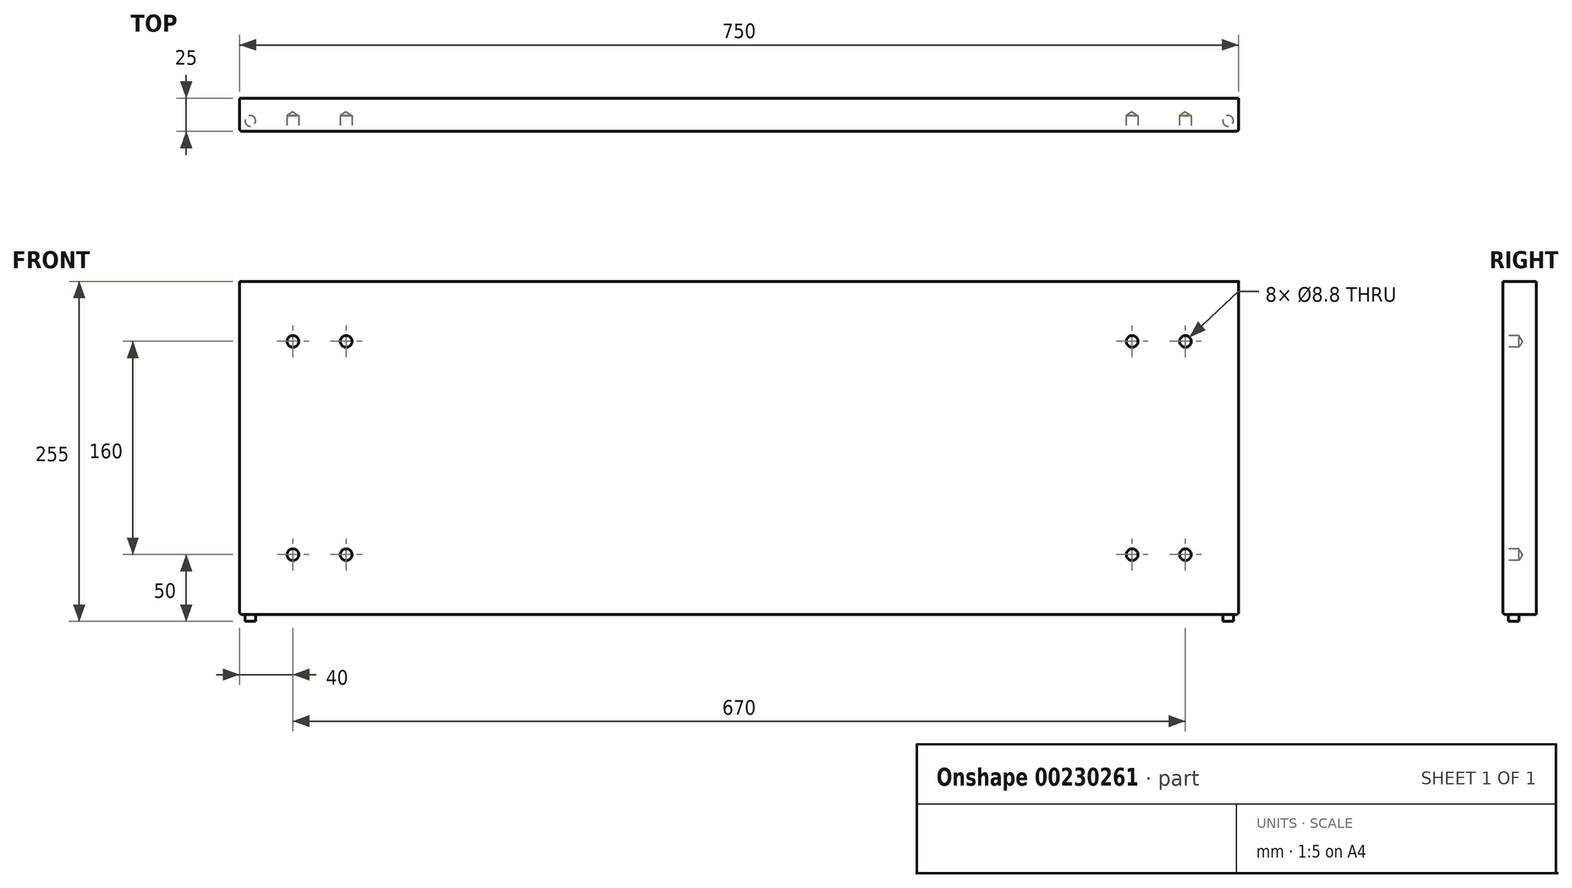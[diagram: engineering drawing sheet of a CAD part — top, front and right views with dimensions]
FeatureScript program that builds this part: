
annotation { "Feature Type Name" : "Feature", "Feature Type Description" : "" }
export const myFeature = defineFeature(function(context is Context, id is Id, definition is map)
    precondition{}
    {
        {
            var Q0;
            Q0=qCreatedBy(makeId("Front.planeOp"),FACE);
            var sketch = newSketch(context, id + "F0", { "sketchPlane" : qUnion([Q0])});
            skLineSegment(sketch, "E0.bottom", {"start": v(375, -125) * mm, "end": v(-375, -125) * mm});
            skLineSegment(sketch, "E0.top", {"start": v(375, 125) * mm, "end": v(-375, 125) * mm});
            skLineSegment(sketch, "E0.left", {"start": v(375, -125) * mm, "end": v(375, 125) * mm});
            skLineSegment(sketch, "E0.right", {"start": v(-375, -125) * mm, "end": v(-375, 125) * mm});
            skPoint(sketch, "E0.middle", {"position": v(0, 0) * mm});
            skSolve(sketch);
        }
        {
            var Q0;
            Q0=makeQuery(id+"F0.imprint","IMPRINT",FACE,{"disambiguationData":[TD([[makeQuery(id+"F0.imprint","IMPRINT",EDGE,{"derivedFrom":sQuery(id+"F0.wireOp",EDGE,"E0.bottom")}),-1.0]])]});
            extrude(context, id + "F1", {"entities" : qUnion([Q0]), "depth" : 25 * mm});
        }
        {
            var Q0;
            Q0=makeQuery(id+"F1.opExtrude","SWEPT_FACE",FACE,{"disambiguationData":[OSD([sQuery(id+"F0.wireOp",EDGE,"E0.bottom")])]});
            var sketch = newSketch(context, id + "F2", { "sketchPlane" : qUnion([Q0])});
            skCircle(sketch, "E1", {"center": v(-367, 17) * mm, "radius": 4 * mm});
            skCircle(sketch, "E2", {"center": v(367, 17) * mm, "radius": 4 * mm});
            skSolve(sketch);
        }
        {
            var Q0;
            Q0=makeQuery(id+"F2.imprint","IMPRINT",FACE,{"disambiguationData":[TD([[makeQuery(id+"F2.imprint","IMPRINT",EDGE,{"derivedFrom":sQuery(id+"F2.wireOp",EDGE,"E1")}),1.0]])]});
            var Q1;
            Q1=makeQuery(id+"F2.imprint","IMPRINT",FACE,{"disambiguationData":[TD([[makeQuery(id+"F2.imprint","IMPRINT",EDGE,{"derivedFrom":sQuery(id+"F2.wireOp",EDGE,"E2")}),1.0]])]});
            extrude(context, id + "F3", {"entities" : qUnion([Q0, Q1]), "operationType" : NewBodyOperationType.ADD, "depth" : 5 * mm});
        }
        {
            var Q0;
            Q0=makeQuery(id+"F1.opExtrude","CAP_EDGE",EDGE,{"disambiguationData":[OSD([sQuery(id+"F0.wireOp",EDGE,"E0.bottom")])],"isStart":false});
            fillet(context, id + "F4", {"entities" : qUnion([Q0]), "radius" : 2 * mm, "tangentPropagation" : true, "allowEdgeOverflow" : false});
        }
        {
            var Q0;
            Q0=makeQuery(id+"F1.opExtrude","SWEPT_EDGE",EDGE,{"disambiguationData":[OSD([sQuery(id+"F0.wireOp",EDGE,"E0.bottom"),sQuery(id+"F0.wireOp",EDGE,"E0.right")])]});
            var Q1;
            Q1=makeQuery(id+"F1.opExtrude","SWEPT_EDGE",EDGE,{"disambiguationData":[OSD([sQuery(id+"F0.wireOp",EDGE,"E0.bottom"),sQuery(id+"F0.wireOp",EDGE,"E0.left")])]});
            fillet(context, id + "F5", {"entities" : qUnion([Q0, Q1]), "radius" : 2 * mm, "tangentPropagation" : true, "allowEdgeOverflow" : false});
        }
        {
            var Q0;
            Q0=makeQuery(id+"F1.opExtrude","CAP_FACE",FACE,{"disambiguationData":[OSD([sQuery(id+"F0.wireOp",EDGE,"E0.bottom"),sQuery(id+"F0.wireOp",EDGE,"E0.top"),sQuery(id+"F0.wireOp",EDGE,"E0.left"),sQuery(id+"F0.wireOp",EDGE,"E0.right")])],"isStart":false});
            var sketch = newSketch(context, id + "F6", { "sketchPlane" : qUnion([Q0])});
            skPoint(sketch, "E3", {"position": v(-335, 80) * mm});
            skPoint(sketch, "E4", {"position": v(-335, -80) * mm});
            skPoint(sketch, "E5", {"position": v(-295, 80) * mm});
            skPoint(sketch, "E6", {"position": v(-295, -80) * mm});
            skPoint(sketch, "E7", {"position": v(295, 80) * mm});
            skPoint(sketch, "E8", {"position": v(335, 80) * mm});
            skPoint(sketch, "E9", {"position": v(295, -80) * mm});
            skPoint(sketch, "E10", {"position": v(335, -80) * mm});
            skSolve(sketch);
        }
        {
            var Q0;
            Q0=sQuery(id+"F6.wireOp",VERTEX,"E3");
            var Q1;
            Q1=sQuery(id+"F6.wireOp",VERTEX,"E5");
            var Q2;
            Q2=sQuery(id+"F6.wireOp",VERTEX,"E6");
            var Q3;
            Q3=sQuery(id+"F6.wireOp",VERTEX,"E4");
            var Q4;
            Q4=sQuery(id+"F6.wireOp",VERTEX,"E7");
            var Q5;
            Q5=sQuery(id+"F6.wireOp",VERTEX,"E8");
            var Q6;
            Q6=sQuery(id+"F6.wireOp",VERTEX,"E9");
            var Q7;
            Q7=sQuery(id+"F6.wireOp",VERTEX,"E10");
            var Q8;
            Q8=makeQuery(id+"F1.opExtrude","SWEPT_BODY",BODY,{"disambiguationData":[OSD([sQuery(id+"F0.wireOp",EDGE,"E0.bottom"),sQuery(id+"F0.wireOp",EDGE,"E0.top"),sQuery(id+"F0.wireOp",EDGE,"E0.left"),sQuery(id+"F0.wireOp",EDGE,"E0.right")])]});
            hole(context, id + "F7", {"style" : HoleStyle.SIMPLE, "endStyle" : HoleEndStyle.BLIND, "standardTappedOrClearance" : lookupTablePath({ "standard" : "ISO", "fit" : "Normal", "size" : "M8", "type" : "Clearance" }), "standardBlindInLast" : lookupTablePath({ "fit" : "Standard", "standard" : "ISO", "size" : "M8", "type" : "Clearance" }), "holeDiameter" : 8.8 * mm, "holeDepth" : 12 * mm, "locations" : qUnion([Q0, Q1, Q2, Q3, Q4, Q5, Q6, Q7]), "scope" : qUnion([Q8])});
        }
    });
